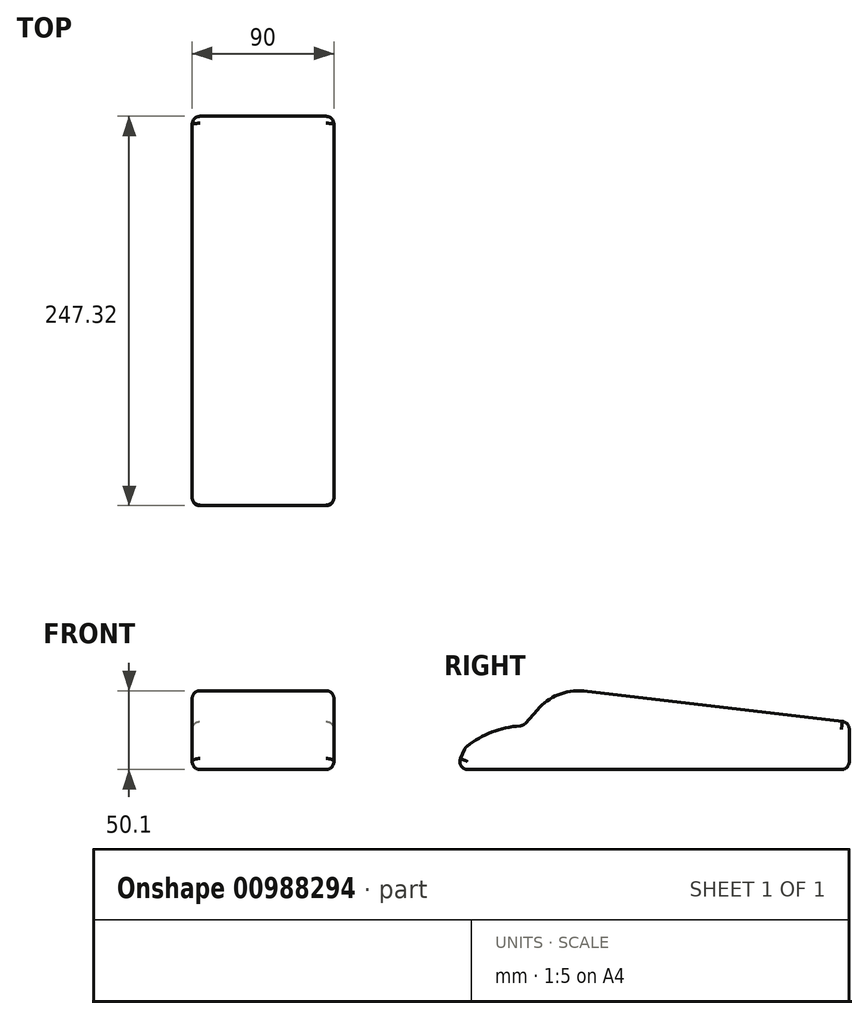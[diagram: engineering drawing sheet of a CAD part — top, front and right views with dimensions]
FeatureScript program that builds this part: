
annotation { "Feature Type Name" : "Feature", "Feature Type Description" : "" }
export const myFeature = defineFeature(function(context is Context, id is Id, definition is map)
    precondition{}
    {
        {
            var Q0;
            Q0=qCreatedBy(makeId("Right.planeOp"),FACE);
            var sketch = newSketch(context, id + "F0", { "sketchPlane" : qUnion([Q0])});
            skLineSegment(sketch, "E0", {"start": v(0, 0) * mm, "end": v(250, 0) * mm});
            skLineSegment(sketch, "E1", {"start": v(250, 0) * mm, "end": v(250, 30) * mm});
            skLineSegment(sketch, "E2", {"start": v(250, 30) * mm, "end": v(81.18, 50) * mm});
            skLineSegment(sketch, "E3", {"start": v(0, 0) * mm, "end": v(6.2, 14) * mm});
            skArc(sketch, "E4", {"start": v(42.87, 27.85) * mm, "mid": v(23.4, 23.94) * mm, "end": v(6.2, 14) * mm});
            skLineSegment(sketch, "E5", {"start": v(42.87, 27.85) * mm, "end": v(51.84, 38.04) * mm});
            skArc(sketch, "E6", {"start": v(81.18, 50) * mm, "mid": v(65.1, 47.47) * mm, "end": v(51.84, 38.04) * mm});
            skSolve(sketch);
        }
        {
            var Q0;
            Q0=makeQuery(id+"F0.imprint","IMPRINT",FACE,{"disambiguationData":[TD([[makeQuery(id+"F0.imprint","IMPRINT",EDGE,{"derivedFrom":sQuery(id+"F0.wireOp",EDGE,"E0")}),1.0]])]});
            var Q1;
            {var subQ0=sQuery(id+"F0.wireOp",EDGE,"1R68XPx9-J5zu-Cyw0-4Fol-crKmPpiqpBY1");Q1=makeQuery(id+"F0.imprint","IMPRINT",FACE,{"disambiguationData":[TD([[makeQuery(id+"F0.imprint","IMPRINT",EDGE,{"derivedFrom":subQ0}),-1.0]])]});}
            var Q2;
            {var subQ2=sQuery(id+"F0.wireOp",EDGE,"YVsCPmW2-w902-yXjp-exVR-MayMz0TvfJcs");Q2=makeQuery(id+"F0.imprint","IMPRINT",FACE,{"disambiguationData":[TD([[makeQuery(id+"F0.imprint","IMPRINT",EDGE,{"derivedFrom":subQ2}),-1.0]])]});}
            var Q3;
            {var subQ0=sQuery(id+"F0.wireOp",EDGE,"pJQmKCXt-Jugd-8LKV-UwA9-3Fh2hMHhbYD1");Q3=makeQuery(id+"F0.imprint","IMPRINT",FACE,{"disambiguationData":[TD([[makeQuery(id+"F0.imprint","IMPRINT",EDGE,{"derivedFrom":subQ0}),-1.0]])]});}
            var Q4;
            Q4=makeQuery(id+"F0.imprint","IMPRINT",FACE,{"disambiguationData":[TD([[makeQuery(id+"F0.imprint","IMPRINT",EDGE,{"derivedFrom":sQuery(id+"F0.wireOp",EDGE,"2rq2Ze2p-yZhJ-ytKn-wDH4-X07GKdA82wF2")}),-1.0]])]});
            extrude(context, id + "F1", {"entities" : qUnion([Q0, Q1, Q2, Q3, Q4]), "depth" : 45 * mm, "offsetDistance" : 25 * mm});
        }
        {
            var Q0;
            Q0=makeQuery(id+"F1.opExtrude","SWEPT_BODY",BODY,{"disambiguationData":[OSD([sQuery(id+"F0.wireOp",EDGE,"E0"),sQuery(id+"F0.wireOp",EDGE,"E1"),sQuery(id+"F0.wireOp",EDGE,"SBPoLh5D-yX3f-GBZE-ytFr-wwVz3jSFbHQM"),sQuery(id+"F0.wireOp",EDGE,"1dE6Ocyv-DW6g-vEmd-QRFU-PrPj86vBe7yQ"),sQuery(id+"F0.wireOp",EDGE,"1R68XPx9-J5zu-Cyw0-4Fol-crKmPpiqpBY1"),sQuery(id+"F0.wireOp",EDGE,"JBpqMCrU-oDk1-t0C3-rqze-gZBAxcPvATLd"),sQuery(id+"F0.wireOp",EDGE,"SJri0J5a-q0Ux-GWB3-RsLh-K1Ex7PpR5GLo"),sQuery(id+"F0.wireOp",EDGE,"E2"),sQuery(id+"F0.wireOp",EDGE,"w8JEsCBl-Okg7-87sl-HOHs-KSCa2yqv3cnt")])]});
            var Q1;
            Q1=qCreatedBy(makeId("Right.planeOp"),FACE);
            mirror(context, id + "F2", {"operationType" : NewBodyOperationType.ADD, "entities" : qUnion([Q0]), "mirrorPlane" : qUnion([Q1])});
        }
        {
            var Q0;
            Q0=makeQuery(id+"F1.opExtrude","CAP_EDGE",EDGE,{"disambiguationData":[OSD([sQuery(id+"F0.wireOp",EDGE,"E2")])],"isStart":false});
            var Q1;
            Q1=makeQuery(id+"F2.opPattern","COPY",EDGE,{"derivedFrom":makeQuery(id+"F1.opExtrude","CAP_EDGE",EDGE,{"disambiguationData":[OSD([sQuery(id+"F0.wireOp",EDGE,"E2")])],"isStart":false}),"instanceName":"1"});
            var Q2;
            Q2=makeQuery(id+"F2.opPattern","COPY",EDGE,{"derivedFrom":makeQuery(id+"F1.opExtrude","CAP_EDGE",EDGE,{"disambiguationData":[OSD([sQuery(id+"F0.wireOp",EDGE,"E6")])],"isStart":false}),"instanceName":"1"});
            var Q3;
            Q3=makeQuery(id+"F2.opPattern","COPY",EDGE,{"derivedFrom":makeQuery(id+"F1.opExtrude","CAP_EDGE",EDGE,{"disambiguationData":[OSD([sQuery(id+"F0.wireOp",EDGE,"E4")])],"isStart":false}),"instanceName":"1"});
            var Q4;
            Q4=makeQuery(id+"F2.opPattern","COPY",EDGE,{"derivedFrom":makeQuery(id+"F1.opExtrude","CAP_EDGE",EDGE,{"disambiguationData":[OSD([sQuery(id+"F0.wireOp",EDGE,"E3")])],"isStart":false}),"instanceName":"1"});
            var Q5;
            Q5=makeQuery(id+"F1.opExtrude","CAP_EDGE",EDGE,{"disambiguationData":[OSD([sQuery(id+"F0.wireOp",EDGE,"E6")])],"isStart":false});
            var Q6;
            Q6=makeQuery(id+"F1.opExtrude","CAP_EDGE",EDGE,{"disambiguationData":[OSD([sQuery(id+"F0.wireOp",EDGE,"E5")])],"isStart":false});
            var Q7;
            Q7=makeQuery(id+"F1.opExtrude","CAP_EDGE",EDGE,{"disambiguationData":[OSD([sQuery(id+"F0.wireOp",EDGE,"E4")])],"isStart":false});
            var Q8;
            Q8=makeQuery(id+"F1.opExtrude","CAP_EDGE",EDGE,{"disambiguationData":[OSD([sQuery(id+"F0.wireOp",EDGE,"E3")])],"isStart":false});
            var Q9;
            {var subQ0=makeQuery(id+"F1.opExtrude","SWEPT_EDGE",EDGE,{"disambiguationData":[OSD([sQuery(id+"F0.wireOp",EDGE,"E3"),sQuery(id+"F0.wireOp",EDGE,"E4")])]});Q9=makeQuery(id+"F2.boolean.opBoolean","MERGE",EDGE,{"derivedFrom":[subQ0,makeQuery(id+"F2.opPattern","COPY",EDGE,{"derivedFrom":subQ0,"instanceName":"1"})]});}
            var Q10;
            {var subQ0=makeQuery(id+"F1.opExtrude","SWEPT_EDGE",EDGE,{"disambiguationData":[OSD([sQuery(id+"F0.wireOp",EDGE,"E5"),sQuery(id+"F0.wireOp",EDGE,"E6")])]});Q10=makeQuery(id+"F2.boolean.opBoolean","MERGE",EDGE,{"derivedFrom":[subQ0,makeQuery(id+"F2.opPattern","COPY",EDGE,{"derivedFrom":subQ0,"instanceName":"1"})]});}
            var Q11;
            {var subQ0=makeQuery(id+"F1.opExtrude","SWEPT_EDGE",EDGE,{"disambiguationData":[OSD([sQuery(id+"F0.wireOp",EDGE,"E4"),sQuery(id+"F0.wireOp",EDGE,"E5")])]});Q11=makeQuery(id+"F2.boolean.opBoolean","MERGE",EDGE,{"derivedFrom":[subQ0,makeQuery(id+"F2.opPattern","COPY",EDGE,{"derivedFrom":subQ0,"instanceName":"1"})]});}
            var Q12;
            {var subQ0=makeQuery(id+"F1.opExtrude","SWEPT_EDGE",EDGE,{"disambiguationData":[OSD([sQuery(id+"F0.wireOp",EDGE,"E2"),sQuery(id+"F0.wireOp",EDGE,"E6")])]});Q12=makeQuery(id+"F2.boolean.opBoolean","MERGE",EDGE,{"derivedFrom":[subQ0,makeQuery(id+"F2.opPattern","COPY",EDGE,{"derivedFrom":subQ0,"instanceName":"1"})]});}
            var Q13;
            {var subQ0=makeQuery(id+"F1.opExtrude","SWEPT_EDGE",EDGE,{"disambiguationData":[OSD([sQuery(id+"F0.wireOp",EDGE,"E1"),sQuery(id+"F0.wireOp",EDGE,"E2")])]});Q13=makeQuery(id+"F2.boolean.opBoolean","MERGE",EDGE,{"derivedFrom":[subQ0,makeQuery(id+"F2.opPattern","COPY",EDGE,{"derivedFrom":subQ0,"instanceName":"1"})]});}
            var Q14;
            {var subQ0=makeQuery(id+"F1.opExtrude","SWEPT_EDGE",EDGE,{"disambiguationData":[OSD([sQuery(id+"F0.wireOp",EDGE,"E0"),sQuery(id+"F0.wireOp",EDGE,"E1")])]});Q14=makeQuery(id+"F2.boolean.opBoolean","MERGE",EDGE,{"derivedFrom":[subQ0,makeQuery(id+"F2.opPattern","COPY",EDGE,{"derivedFrom":subQ0,"instanceName":"1"})]});}
            fillet(context, id + "F3", {"entities" : qUnion([Q0, Q1, Q2, Q3, Q4, Q5, Q6, Q7, Q8, Q9, Q10, Q11, Q12, Q13, Q14]), "radius" : 5 * mm, "tangentPropagation" : true, "allowEdgeOverflow" : false});
        }
        {
            var Q0;
            Q0=makeQuery(id+"F2.opPattern","COPY",EDGE,{"derivedFrom":makeQuery(id+"F1.opExtrude","CAP_EDGE",EDGE,{"disambiguationData":[OSD([sQuery(id+"F0.wireOp",EDGE,"E1")])],"isStart":false}),"instanceName":"1"});
            fillet(context, id + "F4", {"entities" : qUnion([Q0]), "radius" : 5 * mm, "tangentPropagation" : true, "allowEdgeOverflow" : false});
        }
    });
